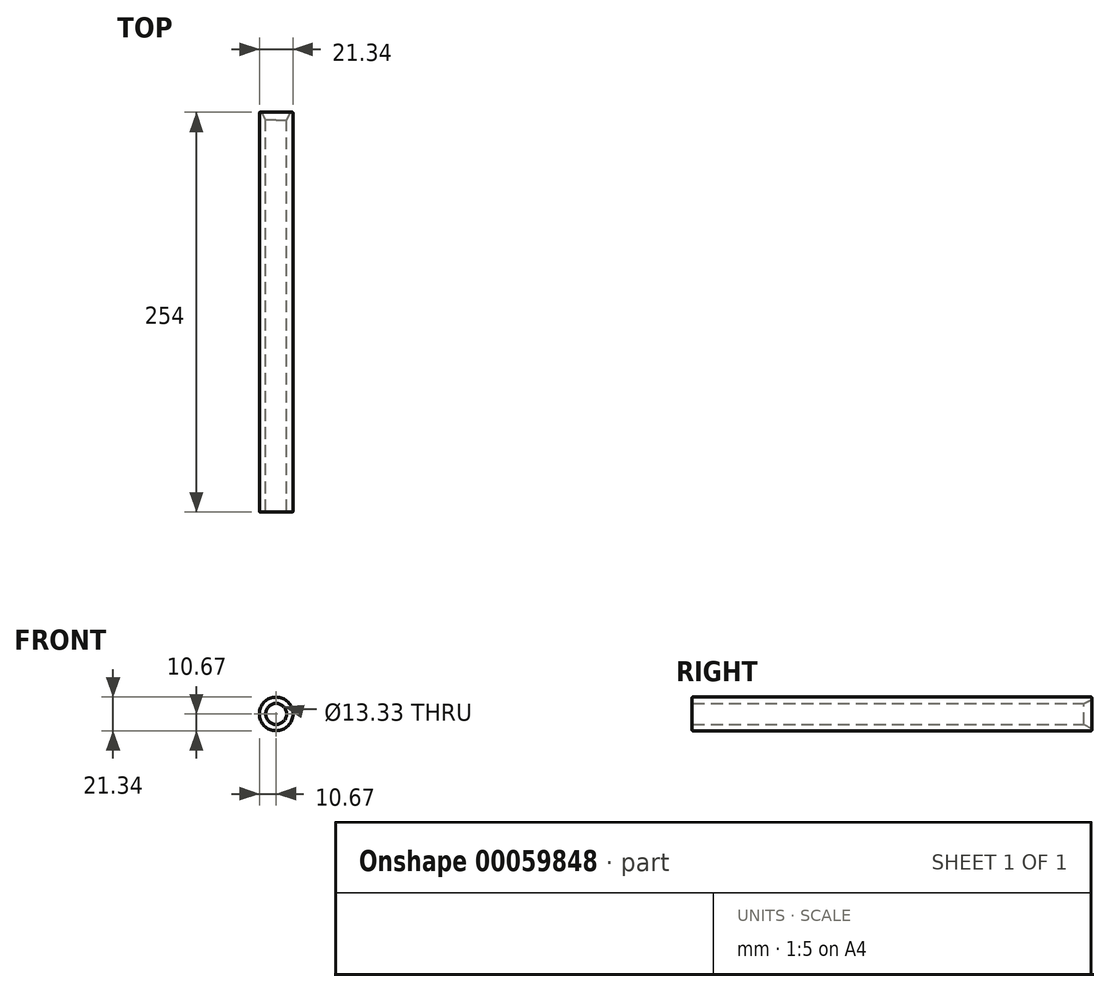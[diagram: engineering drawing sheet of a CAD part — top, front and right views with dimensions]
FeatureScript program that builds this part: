
annotation { "Feature Type Name" : "Feature", "Feature Type Description" : "" }
export const myFeature = defineFeature(function(context is Context, id is Id, definition is map)
    precondition{}
    {
        {
            var Q0;
            Q0=qCreatedBy(makeId("Front.planeOp"),FACE);
            var sketch = newSketch(context, id + "F0", { "sketchPlane" : qUnion([Q0])});
            skCircle(sketch, "E0", {"center": v(0, 0) * mm, "radius": 6.67 * mm});
            skCircle(sketch, "E1", {"center": v(0, 0) * mm, "radius": 10.67 * mm});
            skSolve(sketch);
        }
        {
            var Q0;
            Q0=makeQuery(id+"F0.imprint","IMPRINT",FACE,{"disambiguationData":[TD([[makeQuery(id+"F0.imprint","IMPRINT",EDGE,{"derivedFrom":sQuery(id+"F0.wireOp",EDGE,"E0")}),-1.0]])]});
            extrude(context, id + "F1", {"entities" : qUnion([Q0]), "depth" : 254 * mm});
        }
        {
            var Q0;
            Q0=makeQuery(id+"F1.opExtrude","CAP_EDGE",EDGE,{"disambiguationData":[OSD([sQuery(id+"F0.wireOp",EDGE,"E0")])],"isStart":true});
            chamfer(context, id + "F2", {"entities" : qUnion([Q0]), "chamferType" : ChamferType.TWO_OFFSETS, "width1" : 2.54 * mm, "oppositeDirection" : false, "width2" : 5.08 * mm});
        }
        {
            var Q0;
            Q0=makeQuery(id+"F1.opExtrude","CAP_EDGE",EDGE,{"disambiguationData":[OSD([sQuery(id+"F0.wireOp",EDGE,"E1")])],"isStart":true});
            var Q1;
            {var subQ0=sQuery(id+"F0.wireOp",EDGE,"E0");Q1=makeQuery(id+"F2.opChamfer","BLEND_EDGE",EDGE,{"blendedFrom":[makeQuery(id+"F1.opExtrude","CAP_EDGE",EDGE,{"disambiguationData":[OSD([subQ0])],"isStart":true}),makeQuery(id+"F1.opExtrude","CAP_FACE",FACE,{"disambiguationData":[OSD([subQ0,sQuery(id+"F0.wireOp",EDGE,"E1")])],"isStart":true})],"blendedInto":[makeQuery(id+"F1.opExtrude","CAP_FACE",FACE,{"disambiguationData":[OSD([subQ0,sQuery(id+"F0.wireOp",EDGE,"E1")])],"isStart":true})]});}
            fillet(context, id + "F3", {"entities" : qUnion([Q0, Q1]), "radius" : 0.5 * mm, "tangentPropagation" : true, "allowEdgeOverflow" : false});
        }
        {
            var Q0;
            Q0=makeQuery(id+"F1.opExtrude","CAP_FACE",FACE,{"disambiguationData":[OSD([sQuery(id+"F0.wireOp",EDGE,"E0"),sQuery(id+"F0.wireOp",EDGE,"E1")])],"isStart":false});
            fillet(context, id + "F4", {"entities" : qUnion([Q0]), "radius" : 0.5 * mm, "tangentPropagation" : true, "allowEdgeOverflow" : false});
        }
    });
